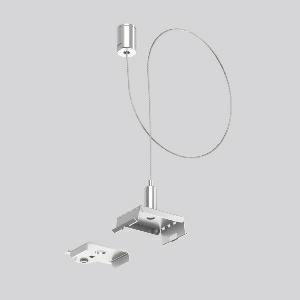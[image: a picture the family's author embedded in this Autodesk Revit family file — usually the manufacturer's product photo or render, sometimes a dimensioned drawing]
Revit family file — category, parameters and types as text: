
# Revit family: linedo_pendelset_1_5m_seil_982661_000_f43f
name_source: partatom
category: Lighting Fixtures
units: mm (PartAtom-declared; Revit-internal decimal feet)

## family parameters
Cut with Voids When Loaded = No
Host = Face
Light Source = No
Part Type = Normal
Room Calculation Point = No
Round Connector Dimension = Use Diameter
Shared = No

## types (1)
- LINEDO Pendelset 1,5m Seil
    Apparent Load = 0 VA
    Default Elevation = 1800 mm
    Description = Suspension kit with steel cable 1,500 mm. Spring steel, blank, for installing continuous line luminaire modules.
Colour: stainless steel
Weight: 51 g
Type of Installation: pendant
    Height = 16 mm
    Lamp = 0 x
    Length = 70 mm
    Luminous efficacy = 0 lm/W
    Manufacturer = RZB
    ModVariant = No
    Model = 982661.000
    Mounting Place = Ceiling
    Mounting Type = Surface mounted
    Number of Poles = 1
    OnlyDefault = Yes
    Power Factor = 1
    Product Name = LINEDO Pendelset 1,5m Seil
    Product group = Surface mounted continuous line luminaire system
    ProductGroupID = 310
    Protection Class = Protection class
    Protection Degree = Degree of protection
    RLX_Detail_Level = 1
    RLX_Emergency_Light_Flux = 0 lm
    RLX_Emergency_Type = 0
    RLX_Emergency_Type_DB = No
    RlxData = <blob elided: 19989 chars, md5=ad52b990>
    Standby Power = 0 W
    System Light Flux = 0 lm
    System Power = 0 W
    Type Comments = Product without accessories
    Type Image = 982661.000.jpg
    URL = http://relux.com
    VarID = ---
    Voltage = 0 V
    Weight = 0.00 kg
    Width = 28 mm

## geometry (parser evidence)
native form markers: Blend x4, Sweep x11
no freeform markers — native parametric forms only
